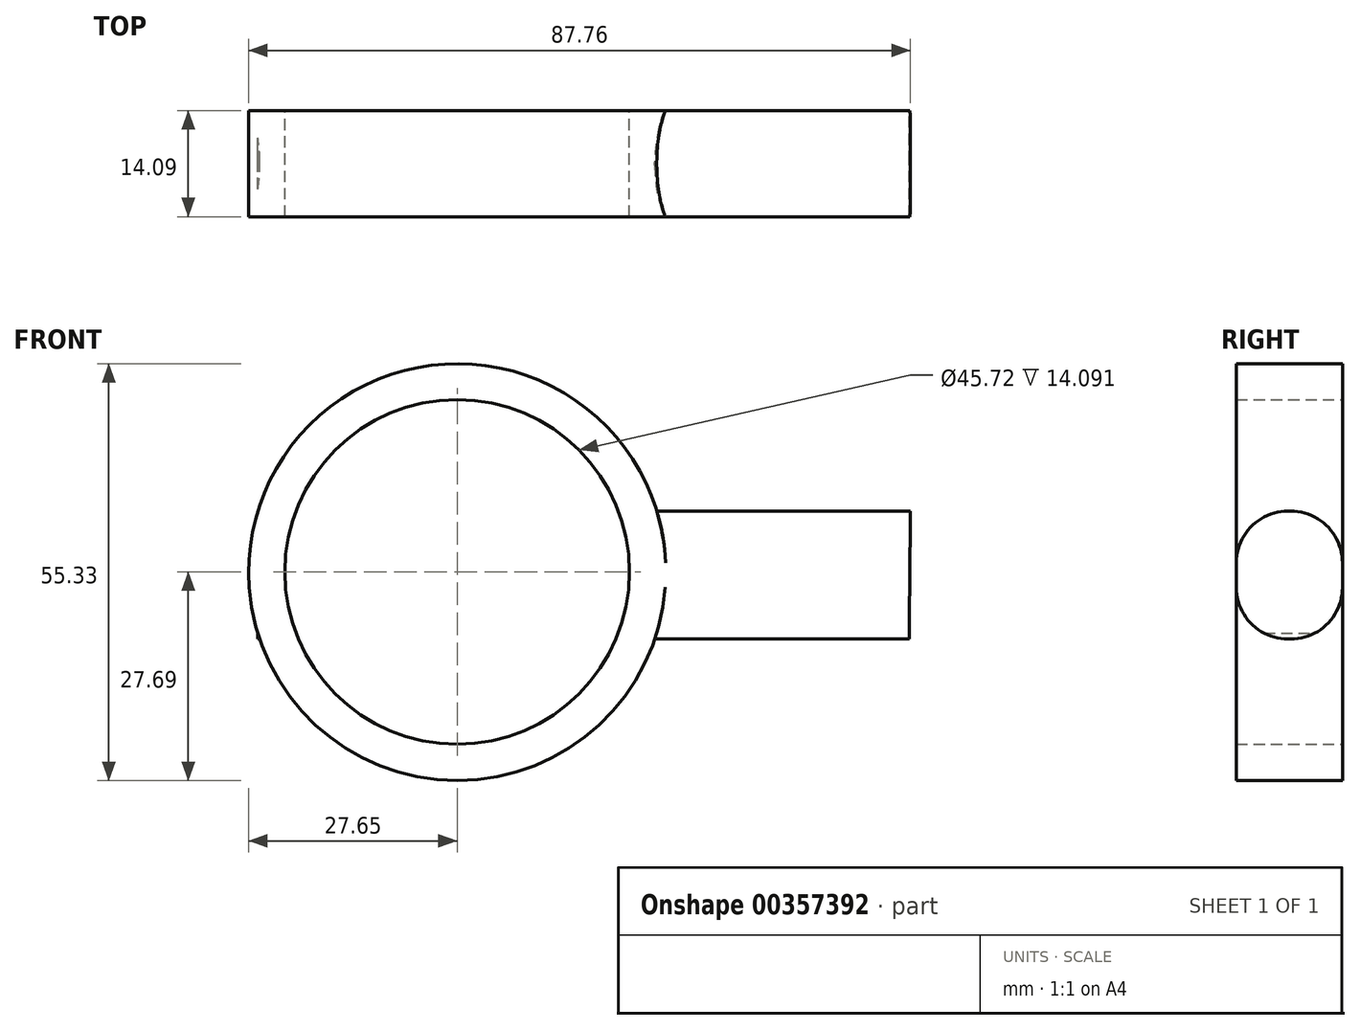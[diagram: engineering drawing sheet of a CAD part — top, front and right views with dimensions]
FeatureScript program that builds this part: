
annotation { "Feature Type Name" : "Feature", "Feature Type Description" : "" }
export const myFeature = defineFeature(function(context is Context, id is Id, definition is map)
    precondition{}
    {
        {
            var Q0;
            Q0=qCreatedBy(makeId("Front.planeOp"),FACE);
            var sketch = newSketch(context, id + "F0", { "sketchPlane" : qUnion([Q0])});
            skCircle(sketch, "E0", {"center": v(0.02, -0.03) * mm, "radius": 27.66 * mm});
            skPoint(sketch, "E0.first.point", {"position": v(27.68, 0) * mm});
            skPoint(sketch, "E0.second.point", {"position": v(-27.65, 0) * mm});
            skPoint(sketch, "E0.third.point", {"position": v(0, -27.7) * mm});
            skLineSegment(sketch, "E1", {"start": v(60.11, 8.07) * mm, "end": v(-26.44, 8.07) * mm});
            skLineSegment(sketch, "E2", {"start": v(-26.44, -8.92) * mm, "end": v(59.95, -8.92) * mm});
            skLineSegment(sketch, "E3", {"start": v(-26.44, 8.07) * mm, "end": v(-26.44, -8.92) * mm});
            skLineSegment(sketch, "E4", {"start": v(60.11, 8.07) * mm, "end": v(59.95, -8.92) * mm});
            skSolve(sketch);
        }
        {
            var Q0;
            Q0 = qSketchRegion(id + "F0", true);
            var Q1;
            Q1=sQuery(id+"F0.wireOp",EDGE,"E0");
            var Q2;
            Q2=sQuery(id+"F0.wireOp",EDGE,"E2");
            var Q3;
            Q3=sQuery(id+"F0.wireOp",EDGE,"E1");
            var Q4;
            Q4=sQuery(id+"F0.wireOp",EDGE,"E3");
            var Q5;
            Q5=sQuery(id+"F0.wireOp",EDGE,"E4");
            extrude(context, id + "F1", {"entities" : qUnion([Q0]), "surfaceEntities" : qUnion([Q1, Q2, Q3, Q4, Q5]), "depth" : 14.1 * mm});
        }
        {
            var Q0;
            Q0=qCreatedBy(makeId("Front.planeOp"),FACE);
            var sketch = newSketch(context, id + "F2", { "sketchPlane" : qUnion([Q0])});
            skPoint(sketch, "E5", {"position": v(0, 0) * mm});
            skSolve(sketch);
        }
        {
            var Q0;
            Q0=sQuery(id+"F2.wireOp",VERTEX,"E5");
            var Q1;
            Q1=makeQuery(id+"F1.opExtrude","SWEPT_BODY",BODY,{"disambiguationData":[OSD([sQuery(id+"F0.wireOp",EDGE,"E0"),sQuery(id+"F0.wireOp",EDGE,"E1"),sQuery(id+"F0.wireOp",EDGE,"E2"),sQuery(id+"F0.wireOp",EDGE,"E3"),sQuery(id+"F0.wireOp",EDGE,"E4")])]});
            hole(context, id + "F3", {"style" : HoleStyle.SIMPLE, "endStyle" : HoleEndStyle.THROUGH, "oppositeDirection" : true, "holeDiameter" : 45.72 * mm, "isTappedThrough" : true, "tappedDepth" : 12.7 * mm, "tapClearance" : 3, "locations" : qUnion([Q0]), "scope" : qUnion([Q1])});
        }
        {
            var Q0;
            {var subQ0=sQuery(id+"F0.wireOp",EDGE,"E2");Q0=makeQuery(id+"F1.opExtrude","CAP_EDGE",EDGE,{"disambiguationData":[OSD([subQ0]),TDD([makeQuery(id+"F0.imprint","IMPRINT",EDGE,{"disambiguationData":[TD([[makeQuery(id+"F0.imprint","INTERSECT",VERTEX,{"derivedFrom":[subQ0,sQuery(id+"F0.wireOp",EDGE,"E4")]}),1.0]])],"derivedFrom":subQ0})])],"isStart":false});}
            var Q1;
            {var subQ0=sQuery(id+"F0.wireOp",EDGE,"E2");Q1=makeQuery(id+"F1.opExtrude","CAP_EDGE",EDGE,{"disambiguationData":[OSD([subQ0]),TDD([makeQuery(id+"F0.imprint","IMPRINT",EDGE,{"disambiguationData":[TD([[makeQuery(id+"F0.imprint","INTERSECT",VERTEX,{"derivedFrom":[subQ0,sQuery(id+"F0.wireOp",EDGE,"E4")]}),1.0]])],"derivedFrom":subQ0})])],"isStart":true});}
            var Q2;
            {var subQ0=sQuery(id+"F0.wireOp",EDGE,"E1");Q2=makeQuery(id+"F1.opExtrude","CAP_EDGE",EDGE,{"disambiguationData":[OSD([subQ0]),TDD([makeQuery(id+"F0.imprint","IMPRINT",EDGE,{"disambiguationData":[TD([[makeQuery(id+"F0.imprint","INTERSECT",VERTEX,{"derivedFrom":[subQ0,sQuery(id+"F0.wireOp",EDGE,"E4")]}),-1.0]])],"derivedFrom":subQ0})])],"isStart":false});}
            var Q3;
            {var subQ0=sQuery(id+"F0.wireOp",EDGE,"E1");Q3=makeQuery(id+"F1.opExtrude","CAP_EDGE",EDGE,{"disambiguationData":[OSD([subQ0]),TDD([makeQuery(id+"F0.imprint","IMPRINT",EDGE,{"disambiguationData":[TD([[makeQuery(id+"F0.imprint","INTERSECT",VERTEX,{"derivedFrom":[subQ0,sQuery(id+"F0.wireOp",EDGE,"E4")]}),-1.0]])],"derivedFrom":subQ0})])],"isStart":true});}
            fillet(context, id + "F4", {"entities" : qUnion([Q0, Q1, Q2, Q3]), "radius" : 6.86 * mm, "tangentPropagation" : true, "allowEdgeOverflow" : false});
        }
        {
            var Q0;
            {var subQ0=sQuery(id+"F0.wireOp",EDGE,"E2");Q0=makeQuery(id+"F1.opExtrude","CAP_EDGE",EDGE,{"disambiguationData":[OSD([subQ0]),TDD([makeQuery(id+"F0.imprint","IMPRINT",EDGE,{"disambiguationData":[TD([[makeQuery(id+"F0.imprint","INTERSECT",VERTEX,{"derivedFrom":[subQ0,sQuery(id+"F0.wireOp",EDGE,"E3")]}),-1.0]])],"derivedFrom":subQ0})])],"isStart":false});}
            var Q1;
            {var subQ0=sQuery(id+"F0.wireOp",EDGE,"E1");Q1=makeQuery(id+"F1.opExtrude","CAP_EDGE",EDGE,{"disambiguationData":[OSD([subQ0]),TDD([makeQuery(id+"F0.imprint","IMPRINT",EDGE,{"disambiguationData":[TD([[makeQuery(id+"F0.imprint","INTERSECT",VERTEX,{"derivedFrom":[subQ0,sQuery(id+"F0.wireOp",EDGE,"E3")]}),1.0]])],"derivedFrom":subQ0})])],"isStart":false});}
            var Q2;
            {var subQ0=sQuery(id+"F0.wireOp",EDGE,"E1");Q2=makeQuery(id+"F1.opExtrude","CAP_EDGE",EDGE,{"disambiguationData":[OSD([subQ0]),TDD([makeQuery(id+"F0.imprint","IMPRINT",EDGE,{"disambiguationData":[TD([[makeQuery(id+"F0.imprint","INTERSECT",VERTEX,{"derivedFrom":[subQ0,sQuery(id+"F0.wireOp",EDGE,"E3")]}),1.0]])],"derivedFrom":subQ0})])],"isStart":true});}
            var Q3;
            {var subQ0=sQuery(id+"F0.wireOp",EDGE,"E2");Q3=makeQuery(id+"F1.opExtrude","CAP_EDGE",EDGE,{"disambiguationData":[OSD([subQ0]),TDD([makeQuery(id+"F0.imprint","IMPRINT",EDGE,{"disambiguationData":[TD([[makeQuery(id+"F0.imprint","INTERSECT",VERTEX,{"derivedFrom":[subQ0,sQuery(id+"F0.wireOp",EDGE,"E3")]}),-1.0]])],"derivedFrom":subQ0})])],"isStart":true});}
            fillet(context, id + "F5", {"entities" : qUnion([Q0, Q1, Q2, Q3]), "radius" : 6.86 * mm, "tangentPropagation" : true, "allowEdgeOverflow" : false});
        }
    });
